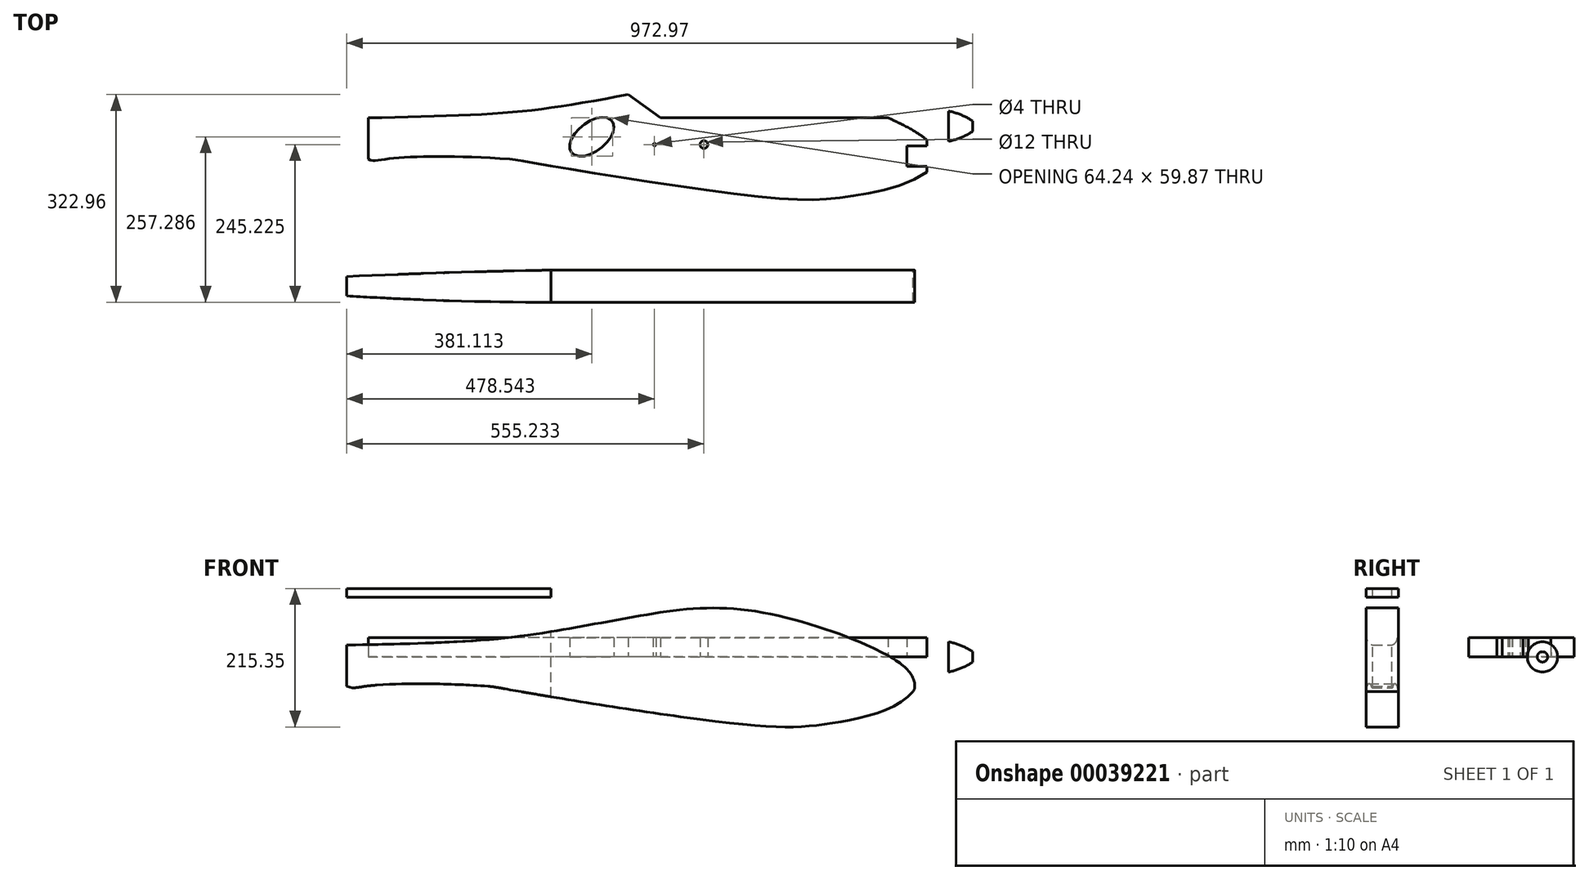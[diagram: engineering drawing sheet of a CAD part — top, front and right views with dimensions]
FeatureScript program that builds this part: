
annotation { "Feature Type Name" : "Feature", "Feature Type Description" : "" }
export const myFeature = defineFeature(function(context is Context, id is Id, definition is map)
    precondition{}
    {
        {
            var Q0;
            Q0=qCreatedBy(makeId("Front.planeOp"),FACE);
            var sketch = newSketch(context, id + "F0", { "sketchPlane" : qUnion([Q0])});
            skLineSegment(sketch, "E0", {"start": v(-641.54, 18.34) * mm, "end": v(238.46, 18.34) * mm});
            skLineSegment(sketch, "E1", {"start": v(-641.54, 18.34) * mm, "end": v(-641.54, -45.72) * mm});
            skFitSpline(sketch, "E2", {"points": [v(238.9, -53.67) * mm, v(117.47, -102.22) * mm, v(-14.88, -105.92) * mm, v(-377.5, -52.88) * mm, v(-421.65, -45.72) * mm], "startDerivative": vector(-318.33, -386.55) * mm, "endDerivative": vector(-180.18, 11.6) * mm});
            skFitSpline(sketch, "E3", {"points": [v(238.9, -53.67) * mm, v(238.9, -33.55) * mm, v(206.7, -2.05) * mm, v(-8.27, 71.16) * mm, v(-190.69, 62.94) * mm, v(-343.1, 36.24) * mm, v(-458.18, 24.2) * mm, v(-641.54, 18.34) * mm], "startDerivative": vector(195.36, 280.51) * mm, "endDerivative": vector(-1108.32, -23.52) * mm});
            skFitSpline(sketch, "E4", {"points": [v(-641.54, -45.72) * mm, v(-612.73, -45.72) * mm, v(-421.65, -45.72) * mm], "startDerivative": vector(72.44, -46.7) * mm, "endDerivative": vector(354.78, -25.1) * mm});
            skLineSegment(sketch, "E5", {"start": v(-92.27, 75.48) * mm, "end": v(-92.27, -97.09) * mm});
            skLineSegment(sketch, "E6", {"start": v(-641.54, 18.34) * mm, "end": v(-641.54, 106.32) * mm});
            skLineSegment(sketch, "E7", {"start": v(-641.54, 106.32) * mm, "end": v(-323.7, 106.32) * mm});
            skLineSegment(sketch, "E8", {"start": v(-323.7, 106.32) * mm, "end": v(-323.7, 92.97) * mm});
            skLineSegment(sketch, "E9", {"start": v(-323.7, 92.97) * mm, "end": v(-641.54, 92.97) * mm});
            skLineSegment(sketch, "E10", {"start": v(238.2, -31.93) * mm, "end": v(-66.8, -31.93) * mm});
            skSolve(sketch);
        }
        {
            var Q0;
            {var subQ5=sQuery(id+"F0.wireOp",EDGE,"E1");Q0=makeQuery(id+"F0.imprint","IMPRINT",FACE,{"disambiguationData":[TD([[makeQuery(id+"F0.imprint","IMPRINT",EDGE,{"derivedFrom":subQ5}),1.0]])]});}
            var Q1;
            {var subQ1=sQuery(id+"F0.wireOp",EDGE,"E0");var subQ5=sQuery(id+"F0.wireOp",EDGE,"E3");var subQ6=makeQuery(id+"F0.imprint","INTERSECT",VERTEX,{"derivedFrom":[subQ1,subQ5]});Q1=makeQuery(id+"F0.imprint","IMPRINT",FACE,{"disambiguationData":[TD([[makeQuery(id+"F0.imprint","IMPRINT",EDGE,{"disambiguationData":[TD([[subQ6,1.0]])],"derivedFrom":subQ1}),-1.0]])]});}
            var Q2;
            {var subQ1=sQuery(id+"F0.wireOp",EDGE,"E0");var subQ3=sQuery(id+"F0.wireOp",EDGE,"E3");var subQ5=makeQuery(id+"F0.imprint","INTERSECT",VERTEX,{"derivedFrom":[subQ1,subQ3]});Q2=makeQuery(id+"F0.imprint","IMPRINT",FACE,{"disambiguationData":[TD([[makeQuery(id+"F0.imprint","IMPRINT",EDGE,{"disambiguationData":[TD([[subQ5,1.0]])],"derivedFrom":subQ1}),1.0]])]});}
            var Q3;
            {var subQ0=sQuery(id+"F0.wireOp",EDGE,"E5");var subQ3=sQuery(id+"F0.wireOp",EDGE,"E3");var subQ4=makeQuery(id+"F0.imprint","INTERSECT",VERTEX,{"derivedFrom":[subQ3,subQ0]});Q3=makeQuery(id+"F0.imprint","IMPRINT",FACE,{"disambiguationData":[TD([[makeQuery(id+"F0.imprint","IMPRINT",EDGE,{"disambiguationData":[TD([[subQ4,-1.0]])],"derivedFrom":subQ0}),-1.0]])]});}
            var Q4;
            {var subQ1=sQuery(id+"F0.wireOp",EDGE,"E7");Q4=makeQuery(id+"F0.imprint","IMPRINT",FACE,{"disambiguationData":[TD([[makeQuery(id+"F0.imprint","IMPRINT",EDGE,{"derivedFrom":subQ1}),-1.0]])]});}
            extrude(context, id + "F1", {"entities" : qUnion([Q0, Q1, Q2, Q3, Q4]), "depth" : 50 * mm});
        }
        {
            var Q0;
            Q0=makeQuery(id+"F1.opExtrude","SWEPT_FACE",FACE,{"disambiguationData":[OSD([sQuery(id+"F0.wireOp",EDGE,"E7")])]});
            var sketch = newSketch(context, id + "F2", { "sketchPlane" : qUnion([Q0])});
            skLineSegment(sketch, "E11", {"start": v(-641.54, -25) * mm, "end": v(-641.54, -40) * mm});
            skLineSegment(sketch, "E12", {"start": v(-641.54, -25) * mm, "end": v(-641.54, -10) * mm});
            skArc(sketch, "E13", {"start": v(-323.7, 0) * mm, "mid": v(-482.66, -3.83) * mm, "end": v(-641.54, -10) * mm});
            skArc(sketch, "E14", {"start": v(-641.54, -40) * mm, "mid": v(-482.7, -47.5) * mm, "end": v(-323.7, -50) * mm});
            skSolve(sketch);
        }
        {
            var Q0;
            {var subQ2=sQuery(id+"F2.wireOp",EDGE,"E13");Q0=makeQuery(id+"F2.imprint","IMPRINT",FACE,{"disambiguationData":[TD([[makeQuery(id+"F2.imprint","IMPRINT",EDGE,{"derivedFrom":subQ2}),-1.0]])]});}
            var Q1;
            {var subQ2=sQuery(id+"F2.wireOp",EDGE,"E14");Q1=makeQuery(id+"F2.imprint","IMPRINT",FACE,{"disambiguationData":[TD([[makeQuery(id+"F2.imprint","IMPRINT",EDGE,{"derivedFrom":subQ2}),-1.0]])]});}
            extrude(context, id + "F3", {"entities" : qUnion([Q0, Q1]), "operationType" : NewBodyOperationType.REMOVE, "oppositeDirection" : true, "depth" : 1500 * mm});
        }
        {
            var Q0;
            Q0=qCreatedBy(makeId("Top.planeOp"),FACE);
            var sketch = newSketch(context, id + "F4", { "sketchPlane" : qUnion([Q0])});
            skLineSegment(sketch, "E15", {"start": v(293.63, 223.81) * mm, "end": v(293.63, 247.31) * mm});
            skLineSegment(sketch, "E16", {"start": v(293.63, 223.81) * mm, "end": v(331.43, 223.81) * mm});
            skLineSegment(sketch, "E17", {"start": v(331.43, 223.81) * mm, "end": v(331.43, 231.81) * mm});
            skArc(sketch, "E18", {"start": v(331.43, 231.81) * mm, "mid": v(313.3, 241.43) * mm, "end": v(293.63, 247.31) * mm});
            skSolve(sketch);
        }
        {
            var Q0;
            Q0=makeQuery(id+"F4.imprint","IMPRINT",FACE,{"disambiguationData":[TD([[makeQuery(id+"F4.imprint","IMPRINT",EDGE,{"derivedFrom":sQuery(id+"F4.wireOp",EDGE,"E15")}),-1.0]])]});
            var Q1;
            Q1=sQuery(id+"F4.wireOp",EDGE,"E16");
            revolve(context, id + "F5", {"entities" : qUnion([Q0]), "axis" : qUnion([Q1]), "revolveType" : RevolveType.FULL});
        }
        {
            var Q0;
            Q0=qCreatedBy(makeId("Top.planeOp"),FACE);
            var sketch = newSketch(context, id + "F6", { "sketchPlane" : qUnion([Q0])});
            skLineSegment(sketch, "E19", {"start": v(-608, 236.72) * mm, "end": v(272, 236.72) * mm});
            skLineSegment(sketch, "E20", {"start": v(-608, 236.72) * mm, "end": v(-608, 172.66) * mm});
            skFitSpline(sketch, "E21", {"points": [v(272.44, 164.71) * mm, v(151, 116.16) * mm, v(18.65, 112.46) * mm, v(-343.96, 165.5) * mm, v(-388.1, 172.66) * mm], "startDerivative": vector(-318.33, -386.55) * mm, "endDerivative": vector(-180.18, 11.6) * mm});
            skFitSpline(sketch, "E22", {"points": [v(272.44, 164.71) * mm, v(272.44, 184.83) * mm, v(240.24, 216.33) * mm, v(25.27, 289.54) * mm, v(-157.15, 281.32) * mm, v(-309.56, 254.62) * mm, v(-424.64, 242.58) * mm, v(-608, 236.72) * mm], "startDerivative": vector(195.36, 280.51) * mm, "endDerivative": vector(-1108.32, -23.52) * mm});
            skFitSpline(sketch, "E23", {"points": [v(-608, 172.66) * mm, v(-579.2, 172.66) * mm, v(-388.1, 172.66) * mm], "startDerivative": vector(72.44, -46.7) * mm, "endDerivative": vector(354.78, -25.1) * mm});
            skLineSegment(sketch, "E24", {"start": v(-608, 236.72) * mm, "end": v(-608, 324.7) * mm});
            skLineSegment(sketch, "E25", {"start": v(-608, 324.7) * mm, "end": v(-290.16, 324.7) * mm});
            skLineSegment(sketch, "E26", {"start": v(-290.16, 324.7) * mm, "end": v(-290.16, 311.35) * mm});
            skLineSegment(sketch, "E27", {"start": v(-290.16, 311.35) * mm, "end": v(-608, 311.35) * mm});
            skLineSegment(sketch, "E28", {"start": v(271.74, 186.45) * mm, "end": v(-8.26, 186.45) * mm});
            skLineSegment(sketch, "E29", {"start": v(276.26, 311.35) * mm, "end": v(276.26, 324.7) * mm});
            skLineSegment(sketch, "E30", {"start": v(276.26, 324.7) * mm, "end": v(-290.16, 324.7) * mm});
            skLineSegment(sketch, "E31", {"start": v(-608, 236.72) * mm, "end": v(-608, 216.72) * mm});
            skLineSegment(sketch, "E32", {"start": v(-608, 216.72) * mm, "end": v(-508, 216.72) * mm});
            skLineSegment(sketch, "E33", {"start": v(-508, 216.72) * mm, "end": v(-508, 208.72) * mm});
            skLineSegment(sketch, "E34", {"start": v(-508, 208.72) * mm, "end": v(-608, 208.72) * mm});
            skLineSegment(sketch, "E35", {"start": v(223.85, 225.38) * mm, "end": v(204.93, 205.37) * mm});
            skLineSegment(sketch, "E36", {"start": v(204.93, 205.37) * mm, "end": v(-153.73, 236.72) * mm});
            skLineSegment(sketch, "E37", {"start": v(-153.73, 236.72) * mm, "end": v(-203.71, 272.96) * mm});
            skLineSegment(sketch, "E38.MirrorCS", {"start": v(-11.04, 195.04) * mm, "end": v(-10.26, 194.4) * mm});
            skLineSegment(sketch, "E39.MirrorCS", {"start": v(-9.19, 191.57) * mm, "end": v(-9.48, 191.17) * mm});
            skLineSegment(sketch, "E40.MirrorCS", {"start": v(-9.37, 193.44) * mm, "end": v(-9.13, 193.01) * mm});
            skLineSegment(sketch, "E41.MirrorCS", {"start": v(-9.9, 190.79) * mm, "end": v(-10.52, 190.37) * mm});
            skLineSegment(sketch, "E42.MirrorCS", {"start": v(-10.26, 194.4) * mm, "end": v(-9.73, 193.87) * mm});
            skLineSegment(sketch, "E43.MirrorCS", {"start": v(-12.72, 189.28) * mm, "end": v(-14.58, 188.6) * mm});
            skLineSegment(sketch, "E44.MirrorCS", {"start": v(-13.89, 196.8) * mm, "end": v(-12.22, 195.85) * mm});
            skLineSegment(sketch, "E45.MirrorCS", {"start": v(-11.4, 189.88) * mm, "end": v(-12.72, 189.28) * mm});
            skLineSegment(sketch, "E46.MirrorCS", {"start": v(-10.52, 190.37) * mm, "end": v(-11.4, 189.88) * mm});
            skLineSegment(sketch, "E47.MirrorCS", {"start": v(-9.73, 193.87) * mm, "end": v(-9.37, 193.44) * mm});
            skLineSegment(sketch, "E48.MirrorCS", {"start": v(-12.22, 195.85) * mm, "end": v(-11.04, 195.04) * mm});
            skLineSegment(sketch, "E49.MirrorCS", {"start": v(-9.48, 191.17) * mm, "end": v(-9.9, 190.79) * mm});
            skLineSegment(sketch, "E50.MirrorCS", {"start": v(-79.03, 183.97) * mm, "end": v(-81.92, 184) * mm});
            skLineSegment(sketch, "E51.MirrorCS", {"start": v(-117.2, 206.46) * mm, "end": v(-114.32, 206.55) * mm});
            skLineSegment(sketch, "E52.MirrorCS", {"start": v(-50.15, 184.34) * mm, "end": v(-53.02, 184.24) * mm});
            skLineSegment(sketch, "E53.MirrorCS", {"start": v(-68.18, 206.36) * mm, "end": v(-65.3, 206.21) * mm});
            skLineSegment(sketch, "E54.MirrorCS", {"start": v(-73.23, 183.95) * mm, "end": v(-76.13, 183.96) * mm});
            skLineSegment(sketch, "E55.MirrorCS", {"start": v(-151.58, 186.52) * mm, "end": v(-154.48, 186.67) * mm});
            skLineSegment(sketch, "E56.MirrorCS", {"start": v(-116.74, 184.9) * mm, "end": v(-119.65, 185.03) * mm});
            skLineSegment(sketch, "E57.MirrorCS", {"start": v(-76.13, 183.96) * mm, "end": v(-79.03, 183.97) * mm});
            skLineSegment(sketch, "E58.MirrorCS", {"start": v(-113.84, 184.8) * mm, "end": v(-116.74, 184.9) * mm});
            skLineSegment(sketch, "E59.MirrorCS", {"start": v(-70.34, 183.95) * mm, "end": v(-73.23, 183.95) * mm});
            skLineSegment(sketch, "E60.MirrorCS", {"start": v(-81.92, 184) * mm, "end": v(-84.82, 184.04) * mm});
            skLineSegment(sketch, "E61.MirrorCS", {"start": v(-55.9, 184.15) * mm, "end": v(-58.78, 184.09) * mm});
            skLineSegment(sketch, "E62.MirrorCS", {"start": v(-67.45, 183.97) * mm, "end": v(-70.34, 183.95) * mm});
            skLineSegment(sketch, "E63.MirrorCS", {"start": v(-71.05, 206.5) * mm, "end": v(-68.18, 206.36) * mm});
            skLineSegment(sketch, "E64.MirrorCS", {"start": v(-108.03, 184.6) * mm, "end": v(-110.94, 184.7) * mm});
            skLineSegment(sketch, "E65.MirrorCS", {"start": v(-79.67, 206.77) * mm, "end": v(-76.8, 206.7) * mm});
            skLineSegment(sketch, "E66.MirrorCS", {"start": v(-87.72, 184.08) * mm, "end": v(-90.62, 184.13) * mm});
            skLineSegment(sketch, "E67.MirrorCS", {"start": v(-53.02, 184.24) * mm, "end": v(-55.9, 184.15) * mm});
            skLineSegment(sketch, "E68.MirrorCS", {"start": v(-145.78, 186.22) * mm, "end": v(-148.68, 186.37) * mm});
            skLineSegment(sketch, "E69.MirrorCS", {"start": v(-114.32, 206.55) * mm, "end": v(-111.42, 206.64) * mm});
            skLineSegment(sketch, "E70.MirrorCS", {"start": v(-73.92, 206.6) * mm, "end": v(-71.05, 206.5) * mm});
            skLineSegment(sketch, "E71.MirrorCS", {"start": v(-142.88, 186.08) * mm, "end": v(-145.78, 186.22) * mm});
            skLineSegment(sketch, "E72.MirrorCS", {"start": v(-84.82, 184.04) * mm, "end": v(-87.72, 184.08) * mm});
            skLineSegment(sketch, "E73.MirrorCS", {"start": v(-111.42, 206.64) * mm, "end": v(-108.53, 206.71) * mm});
            skLineSegment(sketch, "E74.MirrorCS", {"start": v(-65.3, 206.21) * mm, "end": v(-62.45, 206.04) * mm});
            skLineSegment(sketch, "E75.MirrorCS", {"start": v(-110.94, 184.7) * mm, "end": v(-113.84, 184.8) * mm});
            skLineSegment(sketch, "E76.MirrorCS", {"start": v(-76.8, 206.7) * mm, "end": v(-73.92, 206.6) * mm});
            skLineSegment(sketch, "E77.MirrorCS", {"start": v(-108.53, 206.71) * mm, "end": v(-105.64, 206.78) * mm});
            skLineSegment(sketch, "E78.MirrorCS", {"start": v(-105.64, 206.78) * mm, "end": v(-102.75, 206.83) * mm});
            skLineSegment(sketch, "E79.MirrorCS", {"start": v(-169.3, 203.3) * mm, "end": v(-166.4, 203.54) * mm});
            skLineSegment(sketch, "E80.MirrorCS", {"start": v(-105.13, 184.5) * mm, "end": v(-108.03, 184.6) * mm});
            skLineSegment(sketch, "E81.MirrorCS", {"start": v(-82.56, 206.83) * mm, "end": v(-79.67, 206.77) * mm});
            skLineSegment(sketch, "E82.MirrorCS", {"start": v(-27.44, 186.04) * mm, "end": v(-30.23, 185.71) * mm});
            skLineSegment(sketch, "E83.MirrorCS", {"start": v(-94.1, 206.9) * mm, "end": v(-96.98, 206.9) * mm});
            skLineSegment(sketch, "E84.MirrorCS", {"start": v(-85.43, 206.87) * mm, "end": v(-82.56, 206.83) * mm});
            skLineSegment(sketch, "E85.MirrorCS", {"start": v(-61.67, 184.04) * mm, "end": v(-64.56, 184) * mm});
            skLineSegment(sketch, "E86.MirrorCS", {"start": v(-88.32, 206.9) * mm, "end": v(-85.43, 206.87) * mm});
            skLineSegment(sketch, "E87.MirrorCS", {"start": v(-44.4, 184.6) * mm, "end": v(-47.28, 184.46) * mm});
            skLineSegment(sketch, "E88.MirrorCS", {"start": v(-47.28, 184.46) * mm, "end": v(-50.15, 184.34) * mm});
            skLineSegment(sketch, "E89.MirrorCS", {"start": v(-107.64, 206.76) * mm, "end": v(-99.87, 206.87) * mm});
            skLineSegment(sketch, "E90.MirrorCS", {"start": v(-90.62, 184.13) * mm, "end": v(-93.52, 184.2) * mm});
            skLineSegment(sketch, "E91.MirrorCS", {"start": v(-123, 206.24) * mm, "end": v(-120.1, 206.35) * mm});
            skLineSegment(sketch, "E92.MirrorCS", {"start": v(-59.59, 205.85) * mm, "end": v(-56.73, 205.63) * mm});
            skLineSegment(sketch, "E93.MirrorCS", {"start": v(-24.69, 186.42) * mm, "end": v(-27.44, 186.04) * mm});
            skLineSegment(sketch, "E94.MirrorCS", {"start": v(-120.1, 206.35) * mm, "end": v(-117.2, 206.46) * mm});
            skLineSegment(sketch, "E95.MirrorCS", {"start": v(-102.23, 184.42) * mm, "end": v(-105.13, 184.5) * mm});
            skLineSegment(sketch, "E96.MirrorCS", {"start": v(-15.98, 197.8) * mm, "end": v(-13.89, 196.8) * mm});
            skLineSegment(sketch, "E97.MirrorCS", {"start": v(-143.25, 205.2) * mm, "end": v(-140.36, 205.37) * mm});
            skLineSegment(sketch, "E98.MirrorCS", {"start": v(-21.98, 186.87) * mm, "end": v(-24.69, 186.42) * mm});
            skLineSegment(sketch, "E99.MirrorCS", {"start": v(-41.55, 184.77) * mm, "end": v(-44.4, 184.6) * mm});
            skLineSegment(sketch, "E100.MirrorCS", {"start": v(-35.86, 185.18) * mm, "end": v(-38.7, 184.96) * mm});
            skLineSegment(sketch, "E101.MirrorCS", {"start": v(-154.48, 186.67) * mm, "end": v(-157.38, 186.83) * mm});
            skLineSegment(sketch, "E102.MirrorCS", {"start": v(-149.04, 204.83) * mm, "end": v(-146.14, 205.01) * mm});
            skLineSegment(sketch, "E103.MirrorCS", {"start": v(-99.32, 184.33) * mm, "end": v(-102.23, 184.42) * mm});
            skLineSegment(sketch, "E104.MirrorCS", {"start": v(-58.78, 184.09) * mm, "end": v(-61.67, 184.04) * mm});
            skLineSegment(sketch, "E105.MirrorCS", {"start": v(-146.14, 205.01) * mm, "end": v(-143.25, 205.2) * mm});
            skLineSegment(sketch, "E106.MirrorCS", {"start": v(-62.45, 206.04) * mm, "end": v(-59.59, 205.85) * mm});
            skLineSegment(sketch, "E107.MirrorCS", {"start": v(-119.65, 185.03) * mm, "end": v(-122.55, 185.15) * mm});
            skLineSegment(sketch, "E108.MirrorCS", {"start": v(-139.97, 185.93) * mm, "end": v(-142.88, 186.08) * mm});
            skLineSegment(sketch, "E109.MirrorCS", {"start": v(-157.38, 186.83) * mm, "end": v(-160.28, 187) * mm});
            skLineSegment(sketch, "E110.MirrorCS", {"start": v(-38.7, 184.96) * mm, "end": v(-41.55, 184.77) * mm});
            skLineSegment(sketch, "E111.MirrorCS", {"start": v(-18.31, 198.73) * mm, "end": v(-15.98, 197.8) * mm});
            skLineSegment(sketch, "E112.MirrorCS", {"start": v(-30.23, 185.71) * mm, "end": v(-33.04, 185.43) * mm});
            skLineSegment(sketch, "E113.MirrorCS", {"start": v(-64.56, 184) * mm, "end": v(-67.45, 183.97) * mm});
            skLineSegment(sketch, "E114.MirrorCS", {"start": v(-20.8, 199.57) * mm, "end": v(-18.31, 198.73) * mm});
            skLineSegment(sketch, "E115.MirrorCS", {"start": v(-166.08, 187.34) * mm, "end": v(-168.98, 187.51) * mm});
            skLineSegment(sketch, "E116.MirrorCS", {"start": v(-51.04, 205.12) * mm, "end": v(-48.2, 204.82) * mm});
            skLineSegment(sketch, "E117.MirrorCS", {"start": v(-96.42, 184.26) * mm, "end": v(-99.32, 184.33) * mm});
            skLineSegment(sketch, "E118.MirrorCS", {"start": v(-122.55, 185.15) * mm, "end": v(-125.45, 185.27) * mm});
            skLineSegment(sketch, "E119.MirrorCS", {"start": v(-151.93, 204.63) * mm, "end": v(-149.04, 204.83) * mm});
            skLineSegment(sketch, "E120.MirrorCS", {"start": v(-93.52, 184.2) * mm, "end": v(-96.42, 184.26) * mm});
            skLineSegment(sketch, "E121.MirrorCS", {"start": v(-140.36, 205.37) * mm, "end": v(-137.46, 205.53) * mm});
            skLineSegment(sketch, "E122.MirrorCS", {"start": v(-26.02, 201.06) * mm, "end": v(-23.38, 200.35) * mm});
            skLineSegment(sketch, "E123.MirrorCS", {"start": v(-23.38, 200.35) * mm, "end": v(-20.8, 199.57) * mm});
            skLineSegment(sketch, "E124.MirrorCS", {"start": v(-160.28, 187) * mm, "end": v(-163.18, 187.17) * mm});
            skLineSegment(sketch, "E125.MirrorCS", {"start": v(-28.71, 201.7) * mm, "end": v(-26.02, 201.06) * mm});
            skLineSegment(sketch, "E126.MirrorCS", {"start": v(-48.2, 204.82) * mm, "end": v(-45.38, 204.5) * mm});
            skCircle(sketch, "E127.MirrorC", {"center": v(-163, 195.22) * mm, "radius": 2 * mm});
            skLineSegment(sketch, "E128.MirrorCS", {"start": v(-154.82, 204.43) * mm, "end": v(-151.93, 204.63) * mm});
            skLineSegment(sketch, "E129.MirrorCS", {"start": v(-19.34, 187.38) * mm, "end": v(-21.98, 186.87) * mm});
            skLineSegment(sketch, "E130.MirrorCS", {"start": v(-31.44, 202.28) * mm, "end": v(-28.71, 201.7) * mm});
            skLineSegment(sketch, "E131.MirrorCS", {"start": v(-134.17, 185.66) * mm, "end": v(-137.07, 185.8) * mm});
            skLineSegment(sketch, "E132.MirrorCS", {"start": v(-16.84, 187.95) * mm, "end": v(-19.34, 187.38) * mm});
            skLineSegment(sketch, "E133.MirrorCS", {"start": v(-53.89, 205.39) * mm, "end": v(-51.04, 205.12) * mm});
            skLineSegment(sketch, "E134.MirrorCS", {"start": v(-14.58, 188.6) * mm, "end": v(-16.84, 187.95) * mm});
            skLineSegment(sketch, "E135.MirrorCS", {"start": v(-33.04, 185.43) * mm, "end": v(-35.86, 185.18) * mm});
            skLineSegment(sketch, "E136.MirrorCS", {"start": v(-157.72, 204.22) * mm, "end": v(-154.82, 204.43) * mm});
            skLineSegment(sketch, "E137.MirrorCS", {"start": v(-56.73, 205.63) * mm, "end": v(-53.89, 205.39) * mm});
            skLineSegment(sketch, "E138.MirrorCS", {"start": v(-125.45, 185.27) * mm, "end": v(-128.36, 185.4) * mm});
            skLineSegment(sketch, "E139.MirrorCS", {"start": v(-42.56, 204.13) * mm, "end": v(-39.76, 203.73) * mm});
            skLineSegment(sketch, "E140.MirrorCS", {"start": v(-131.68, 205.84) * mm, "end": v(-128.78, 205.98) * mm});
            skLineSegment(sketch, "E141.MirrorCS", {"start": v(-45.38, 204.5) * mm, "end": v(-42.56, 204.13) * mm});
            skLineSegment(sketch, "E142.MirrorCS", {"start": v(-137.46, 205.53) * mm, "end": v(-134.57, 205.69) * mm});
            skLineSegment(sketch, "E143.MirrorCS", {"start": v(-134.57, 205.69) * mm, "end": v(-131.68, 205.84) * mm});
            skLineSegment(sketch, "E144.MirrorCS", {"start": v(-128.36, 185.4) * mm, "end": v(-131.26, 185.52) * mm});
            skLineSegment(sketch, "E145.MirrorCS", {"start": v(-34.2, 202.81) * mm, "end": v(-31.44, 202.28) * mm});
            skLineSegment(sketch, "E146.MirrorCS", {"start": v(-128.78, 205.98) * mm, "end": v(-125.89, 206.11) * mm});
            skLineSegment(sketch, "E147.MirrorCS", {"start": v(-131.26, 185.52) * mm, "end": v(-134.17, 185.66) * mm});
            skLineSegment(sketch, "E148.MirrorCS", {"start": v(-36.97, 203.3) * mm, "end": v(-34.2, 202.81) * mm});
            skLineSegment(sketch, "E149.MirrorCS", {"start": v(-125.89, 206.11) * mm, "end": v(-123, 206.24) * mm});
            skLineSegment(sketch, "E150.MirrorCS", {"start": v(-39.76, 203.73) * mm, "end": v(-36.97, 203.3) * mm});
            skCircle(sketch, "E151.MirrorC", {"center": v(-86.3, 195.22) * mm, "radius": 6 * mm});
            skLineSegment(sketch, "E152.MirrorCS", {"start": v(-86.3, 195.22) * mm, "end": v(-163, 195.22) * mm});
            skLineSegment(sketch, "E153.MirrorCS", {"start": v(-9.13, 193.01) * mm, "end": v(-8.98, 192.48) * mm});
            skLineSegment(sketch, "E154.MirrorCS", {"start": v(-9.01, 191.94) * mm, "end": v(-9.19, 191.57) * mm});
            skLineSegment(sketch, "E155.MirrorCS", {"start": v(-166.4, 203.54) * mm, "end": v(-163.5, 203.77) * mm});
            skLineSegment(sketch, "E156.MirrorCS", {"start": v(-148.68, 186.37) * mm, "end": v(-151.58, 186.52) * mm});
            skLineSegment(sketch, "E157.MirrorCS", {"start": v(-137.07, 185.8) * mm, "end": v(-139.97, 185.93) * mm});
            skLineSegment(sketch, "E158.MirrorCS", {"start": v(-91.2, 206.9) * mm, "end": v(-88.32, 206.9) * mm});
            skLineSegment(sketch, "E159.MirrorCS", {"start": v(-168.98, 187.51) * mm, "end": v(-171.89, 187.7) * mm});
            skLineSegment(sketch, "E160.MirrorCS", {"start": v(-102.75, 206.83) * mm, "end": v(-99.87, 206.87) * mm});
            skLineSegment(sketch, "E161.MirrorCS", {"start": v(-163.18, 187.17) * mm, "end": v(-166.08, 187.34) * mm});
            skLineSegment(sketch, "E162.MirrorCS", {"start": v(-163.5, 203.77) * mm, "end": v(-160.61, 204) * mm});
            skLineSegment(sketch, "E163.MirrorCS", {"start": v(-160.61, 204) * mm, "end": v(-157.72, 204.22) * mm});
            skLineSegment(sketch, "E164.MirrorCS", {"start": v(-180.86, 202.27) * mm, "end": v(-183.76, 202) * mm});
            skLineSegment(sketch, "E165.MirrorCS", {"start": v(-175.07, 202.8) * mm, "end": v(-172.18, 203.05) * mm});
            skLineSegment(sketch, "E166.MirrorCS", {"start": v(-172.18, 203.05) * mm, "end": v(-169.3, 203.3) * mm});
            skLineSegment(sketch, "E167.MirrorCS", {"start": v(-177.97, 202.54) * mm, "end": v(-175.07, 202.8) * mm});
            skLineSegment(sketch, "E168", {"start": v(-8.98, 192.48) * mm, "end": v(-8.94, 192.12) * mm});
            skLineSegment(sketch, "E169", {"start": v(-94.1, 206.9) * mm, "end": v(-91.2, 206.9) * mm});
            skLineSegment(sketch, "E170", {"start": v(-99.87, 206.87) * mm, "end": v(-96.98, 206.9) * mm});
            skLineSegment(sketch, "E171", {"start": v(-180.86, 202.27) * mm, "end": v(-177.97, 202.54) * mm});
            skLineSegment(sketch, "E172", {"start": v(-174.79, 187.87) * mm, "end": v(-176.86, 188) * mm});
            skLineSegment(sketch, "E173", {"start": v(-183.76, 202) * mm, "end": v(-176.86, 188) * mm});
            skLineSegment(sketch, "E174", {"start": v(-8.94, 192.12) * mm, "end": v(-9.01, 191.94) * mm});
            skLineSegment(sketch, "E175", {"start": v(-174.79, 187.87) * mm, "end": v(-171.89, 187.7) * mm});
            skLineSegment(sketch, "E176", {"start": v(274.97, 174.13) * mm, "end": v(259.97, 174.13) * mm});
            skLineSegment(sketch, "E177", {"start": v(259.97, 174.13) * mm, "end": v(259.97, 152.78) * mm});
            skLineSegment(sketch, "E178", {"start": v(259.97, 174.13) * mm, "end": v(259.97, 202.08) * mm});
            skLineSegment(sketch, "E179", {"start": v(259.97, 202.08) * mm, "end": v(259.97, 152.78) * mm});
            skLineSegment(sketch, "E180", {"start": v(259.97, 177.43) * mm, "end": v(228.97, 177.43) * mm});
            skLineSegment(sketch, "E181", {"start": v(228.97, 177.43) * mm, "end": v(228.97, 193.43) * mm});
            skLineSegment(sketch, "E182", {"start": v(228.97, 177.43) * mm, "end": v(228.97, 161.43) * mm});
            skLineSegment(sketch, "E183", {"start": v(228.97, 193.43) * mm, "end": v(259.97, 193.43) * mm});
            skLineSegment(sketch, "E184", {"start": v(228.97, 161.43) * mm, "end": v(259.97, 161.43) * mm});
            skLineSegment(sketch, "E185", {"start": v(228.97, 177.43) * mm, "end": v(208.97, 177.43) * mm});
            skEllipse(sketch, "E186", {"center": v(-260.43, 207.29) * mm, "majorRadius": 39.96 * mm, "minorRadius": 22.59 * mm, "majorAxis": v(-0.8, -0.61)});
            skSolve(sketch);
        }
        {
            var Q0;
            {var subQ1=sQuery(id+"F6.wireOp",EDGE,"E32");Q0=makeQuery(id+"F6.imprint","IMPRINT",FACE,{"disambiguationData":[TD([[makeQuery(id+"F6.imprint","IMPRINT",EDGE,{"derivedFrom":subQ1}),-1.0]])]});}
            var Q1;
            {var subQ19=sQuery(id+"F6.wireOp",EDGE,"E23");Q1=makeQuery(id+"F6.imprint","IMPRINT",FACE,{"disambiguationData":[TD([[makeQuery(id+"F6.imprint","IMPRINT",EDGE,{"derivedFrom":subQ19}),1.0]])]});}
            var Q2;
            {var subQ3=sQuery(id+"F6.wireOp",EDGE,"E37");Q2=makeQuery(id+"F6.imprint","IMPRINT",FACE,{"disambiguationData":[TD([[makeQuery(id+"F6.imprint","IMPRINT",EDGE,{"derivedFrom":subQ3}),1.0]])]});}
            var Q3;
            {var subQ1=sQuery(id+"F6.wireOp",EDGE,"E35");Q3=makeQuery(id+"F6.imprint","IMPRINT",FACE,{"disambiguationData":[TD([[makeQuery(id+"F6.imprint","IMPRINT",EDGE,{"derivedFrom":subQ1}),-1.0]])]});}
            var Q4;
            Q4=makeQuery(id+"F6.imprint","IMPRINT",FACE,{"disambiguationData":[TD([[makeQuery(id+"F6.imprint","IMPRINT",EDGE,{"derivedFrom":sQuery(id+"F6.wireOp",EDGE,"E40.MirrorCS")}),-1.0]])]});
            extrude(context, id + "F7", {"entities" : qUnion([Q0, Q1, Q2, Q3, Q4]), "depth" : 30 * mm});
        }
    });
